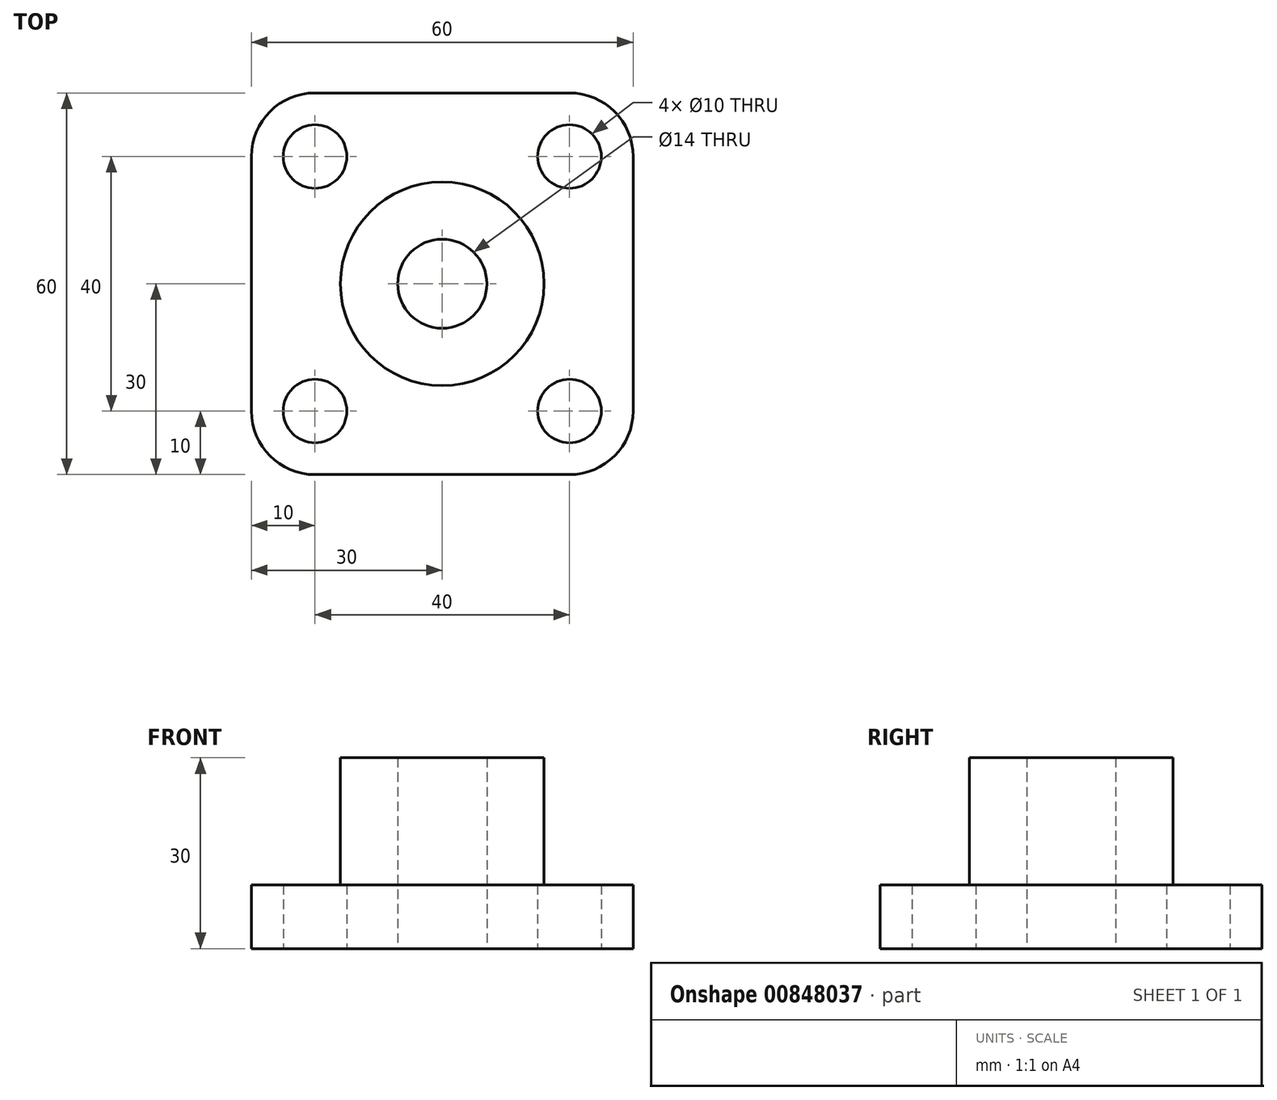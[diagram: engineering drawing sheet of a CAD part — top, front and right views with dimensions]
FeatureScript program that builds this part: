
annotation { "Feature Type Name" : "Feature", "Feature Type Description" : "" }
export const myFeature = defineFeature(function(context is Context, id is Id, definition is map)
    precondition{}
    {
        {
            var Q0;
            Q0=qCreatedBy(makeId("Top.planeOp"),FACE);
            var sketch = newSketch(context, id + "F0", { "sketchPlane" : qUnion([Q0])});
            skLineSegment(sketch, "E0.bottom", {"start": v(30, -30) * mm, "end": v(-30, -30) * mm});
            skLineSegment(sketch, "E0.top", {"start": v(30, 30) * mm, "end": v(-30, 30) * mm});
            skLineSegment(sketch, "E0.left", {"start": v(30, -30) * mm, "end": v(30, 30) * mm});
            skLineSegment(sketch, "E0.right", {"start": v(-30, -30) * mm, "end": v(-30, 30) * mm});
            skPoint(sketch, "E0.middle", {"position": v(0, 0) * mm});
            skCircle(sketch, "E1", {"center": v(0, 0) * mm, "radius": 16 * mm});
            skCircle(sketch, "E2", {"center": v(0, 0) * mm, "radius": 8 * mm});
            skLineSegment(sketch, "E3", {"start": v(0, 0) * mm, "end": v(0, 20) * mm});
            skLineSegment(sketch, "E4", {"start": v(0, 20) * mm, "end": v(20, 20) * mm});
            skLineSegment(sketch, "E5", {"start": v(20, -20) * mm, "end": v(20, 20) * mm});
            skLineSegment(sketch, "E6", {"start": v(20, -20) * mm, "end": v(-20, -20) * mm});
            skLineSegment(sketch, "E7", {"start": v(-20, -20) * mm, "end": v(-20, 20) * mm});
            skCircle(sketch, "E8", {"center": v(-20, 20) * mm, "radius": 5 * mm});
            skCircle(sketch, "E9", {"center": v(20, 20) * mm, "radius": 5 * mm});
            skCircle(sketch, "E10", {"center": v(20, -20) * mm, "radius": 5 * mm});
            skCircle(sketch, "E11", {"center": v(-20, -20) * mm, "radius": 5 * mm});
            skSolve(sketch);
        }
        {
            var Q0;
            Q0=makeQuery(id+"F0.imprint","IMPRINT",FACE,{"disambiguationData":[TD([[makeQuery(id+"F0.imprint","IMPRINT",EDGE,{"derivedFrom":sQuery(id+"F0.wireOp",EDGE,"E0.bottom")}),-1.0]])]});
            extrude(context, id + "F1", {"entities" : qUnion([Q0]), "depth" : 10 * mm, "offsetDistance" : 25 * mm});
        }
        {
            var Q0;
            Q0=makeQuery(id+"F1.opExtrude","SWEPT_EDGE",EDGE,{"disambiguationData":[OSD([sQuery(id+"F0.wireOp",EDGE,"E0.top"),sQuery(id+"F0.wireOp",EDGE,"E0.left")])]});
            var Q1;
            Q1=makeQuery(id+"F1.opExtrude","SWEPT_EDGE",EDGE,{"disambiguationData":[OSD([sQuery(id+"F0.wireOp",EDGE,"E0.top"),sQuery(id+"F0.wireOp",EDGE,"E0.right")])]});
            fillet(context, id + "F2", {"entities" : qUnion([Q0, Q1]), "radius" : 10 * mm, "tangentPropagation" : true, "allowEdgeOverflow" : false});
        }
        {
            var Q0;
            Q0=makeQuery(id+"F1.opExtrude","SWEPT_EDGE",EDGE,{"disambiguationData":[OSD([sQuery(id+"F0.wireOp",EDGE,"E0.bottom"),sQuery(id+"F0.wireOp",EDGE,"E0.left")])]});
            fillet(context, id + "F3", {"entities" : qUnion([Q0]), "radius" : 10 * mm, "tangentPropagation" : true, "allowEdgeOverflow" : false});
        }
        {
            var Q0;
            Q0=makeQuery(id+"F1.opExtrude","SWEPT_EDGE",EDGE,{"disambiguationData":[OSD([sQuery(id+"F0.wireOp",EDGE,"E0.bottom"),sQuery(id+"F0.wireOp",EDGE,"E0.right")])]});
            fillet(context, id + "F4", {"entities" : qUnion([Q0]), "radius" : 10 * mm, "tangentPropagation" : true, "allowEdgeOverflow" : false});
        }
        {
            var Q0;
            Q0=makeQuery(id+"F1.opExtrude","CAP_FACE",FACE,{"disambiguationData":[OSD([sQuery(id+"F0.wireOp",EDGE,"E0.bottom"),sQuery(id+"F0.wireOp",EDGE,"E0.top"),sQuery(id+"F0.wireOp",EDGE,"E0.left"),sQuery(id+"F0.wireOp",EDGE,"E0.right"),sQuery(id+"F0.wireOp",EDGE,"E1"),sQuery(id+"F0.wireOp",EDGE,"E8"),sQuery(id+"F0.wireOp",EDGE,"E9"),sQuery(id+"F0.wireOp",EDGE,"E10"),sQuery(id+"F0.wireOp",EDGE,"E11")])],"isStart":false});
            var sketch = newSketch(context, id + "F5", { "sketchPlane" : qUnion([Q0])});
            skSolve(sketch);
        }
        {
            var Q0;
            Q0=qCreatedBy(makeId("Top.planeOp"),FACE);
            var sketch = newSketch(context, id + "F6", { "sketchPlane" : qUnion([Q0])});
            skCircle(sketch, "E12", {"center": v(0, 0) * mm, "radius": 16 * mm});
            skSolve(sketch);
        }
        {
            var Q0;
            Q0=makeQuery(id+"F1.opExtrude","CAP_FACE",FACE,{"disambiguationData":[OSD([sQuery(id+"F0.wireOp",EDGE,"E0.bottom"),sQuery(id+"F0.wireOp",EDGE,"E0.top"),sQuery(id+"F0.wireOp",EDGE,"E0.left"),sQuery(id+"F0.wireOp",EDGE,"E0.right"),sQuery(id+"F0.wireOp",EDGE,"E1"),sQuery(id+"F0.wireOp",EDGE,"E8"),sQuery(id+"F0.wireOp",EDGE,"E9"),sQuery(id+"F0.wireOp",EDGE,"E10"),sQuery(id+"F0.wireOp",EDGE,"E11")])],"isStart":true});
            var sketch = newSketch(context, id + "F7", { "sketchPlane" : qUnion([Q0])});
            skSolve(sketch);
        }
        {
            var Q0;
            Q0=makeQuery(id+"F7.imprint","IMPRINT",FACE,{"disambiguationData":[TD([[makeQuery(id+"F7.imprint","IMPRINT",EDGE,{"derivedFrom":makeQuery(id+"F1.opExtrude","CAP_EDGE",EDGE,{"disambiguationData":[OSD([sQuery(id+"F0.wireOp",EDGE,"E1")])],"isStart":true})}),-1.0]])]});
            extrude(context, id + "F8", {"entities" : qUnion([Q0]), "operationType" : NewBodyOperationType.ADD, "oppositeDirection" : true, "depth" : 30 * mm, "offsetDistance" : 25 * mm});
        }
        {
            var Q0;
            Q0=sQuery(id+"F6.wireOp",VERTEX,"E12.center");
            var Q1;
            Q1=makeQuery(id+"F1.opExtrude","SWEPT_BODY",BODY,{"disambiguationData":[OSD([sQuery(id+"F0.wireOp",EDGE,"E0.bottom"),sQuery(id+"F0.wireOp",EDGE,"E0.top"),sQuery(id+"F0.wireOp",EDGE,"E0.left"),sQuery(id+"F0.wireOp",EDGE,"E0.right"),sQuery(id+"F0.wireOp",EDGE,"E1"),sQuery(id+"F0.wireOp",EDGE,"E8"),sQuery(id+"F0.wireOp",EDGE,"E9"),sQuery(id+"F0.wireOp",EDGE,"E10"),sQuery(id+"F0.wireOp",EDGE,"E11")])]});
            hole(context, id + "F9", {"style" : HoleStyle.SIMPLE, "endStyle" : HoleEndStyle.THROUGH, "oppositeDirection" : true, "holeDiameter" : 14 * mm, "majorDiameter" : 5 * mm, "isTappedThrough" : true, "tappedDepth" : 12 * mm, "tapClearance" : 3, "locations" : qUnion([Q0]), "scope" : qUnion([Q1])});
        }
    });
